# Revit family: Plumbing_Valves_Bermad_720-EN_Pressure_Reducing_Valve Flanged 1.5in-12in
name_source: partatom
category: Pipe Accessories
units: mm (PartAtom-declared; Revit-internal decimal feet)

## family parameters
Always vertical = Yes
Cut with Voids When Loaded = No
Part Type = Valve - Breaks Into
Round Connector Dimension = Use Diameter
Shared = No
Work Plane-Based = No

## types (9) — shared parameters
700EN = Yes
700ES = No
700Grooved = No
700Threaded = No
Act_Ang = 25.00°
Assembly Code = D2020300
D_Table = 700 Revit Sizes
D_Table_Version = 2
Date of publishing = 26/09/2019
Description = Pressure Reducing Valve
HC = No
M = 160 mm
Manufacturer = Bermad
Max Working Water Pressure = 27.6 bar
Max Working Water Temperature = 60 °C
Model = 720
PA = No
PA_8 = No
PB = No
PBL = Yes
Port_Dim = 40 mm  [stored 0.131234 ft]
Product url = www.bermad.com/product/bc-720-p
Show Actuator Maintenance Space = No
T_from_port = 220 mm
URL = www.Bermad.com
Valve Seires = 700 EN

## per-type parameters (varying)
- 1.5" - DN40: Act_BD=127 mm; Ax=6 mm  [stored 0.019685 ft]; Ay=81 mm; Body_Dim=59 mm  [stored 0.19357 ft]; C_Plus=98 mm; D1=86 mm; D2=125 mm; D3=85 mm; D4=125 mm; D5=86 mm; D6=38 mm  [stored 0.124672 ft]; Flange_Dim=155 mm; Flange_Thick=22 mm  [stored 0.0721785 ft]; H=234 mm; H1=10 mm  [stored 0.0328084 ft]; H2=19 mm  [stored 0.062336 ft]; H3=12 mm  [stored 0.0393701 ft]; H4=32 mm  [stored 0.104987 ft]; H5=9 mm  [stored 0.0295276 ft]; K Coefficient=1.9; L=230 mm; L_Half=115 mm; Nominal Diameter=40 mm  [stored 0.131234 ft]; Port_Downx=57 mm  [stored 0.187008 ft]; Port_Upx=57 mm  [stored 0.187008 ft]; Port_W=49 mm  [stored 0.160761 ft]; Port_W2=98 mm; Port_h=44 mm  [stored 0.144357 ft]; W=155 mm; Weight=0.12 kN; h=81 mm
- 2" - DN50: Act_BD=127 mm; Ax=6 mm  [stored 0.019685 ft]; Ay=81 mm; Body_Dim=60 mm  [stored 0.19685 ft]; C_Plus=98 mm; D1=86 mm; D2=125 mm; D3=85 mm; D4=125 mm; D5=86 mm; D6=38 mm  [stored 0.124672 ft]; Flange_Dim=165 mm; Flange_Thick=24 mm  [stored 0.0787402 ft]; H=246 mm; H1=10 mm  [stored 0.0328084 ft]; H2=19 mm  [stored 0.062336 ft]; H3=12 mm  [stored 0.0393701 ft]; H4=32 mm  [stored 0.104987 ft]; H5=9 mm  [stored 0.0295276 ft]; K Coefficient=4.3; L=230 mm; L_Half=115 mm; Nominal Diameter=50 mm  [stored 0.164042 ft]; Port_Downx=60 mm  [stored 0.19685 ft]; Port_Upx=56 mm  [stored 0.183727 ft]; Port_W=49 mm  [stored 0.160761 ft]; Port_W2=98 mm; Port_h=44 mm  [stored 0.144357 ft]; W=165 mm; Weight=0.14 kN; h=86 mm
- 2.5" - DN65: Act_BD=145 mm; Ax=11 mm; Ay=102 mm; Body_Dim=77 mm; C_Plus=108 mm; D1=94 mm; D2=153 mm; D3=131 mm; D4=165 mm; D5=122 mm; D6=42 mm  [stored 0.137795 ft]; Flange_Dim=190 mm; Flange_Thick=27 mm  [stored 0.0885827 ft]; H=294 mm; H1=16 mm  [stored 0.0524934 ft]; H2=28 mm  [stored 0.0918635 ft]; H3=21 mm  [stored 0.0688976 ft]; H4=28 mm  [stored 0.0918635 ft]; H5=23 mm  [stored 0.0754593 ft]; K Coefficient=5.3; L=290 mm; L_Half=145 mm; Nominal Diameter=65 mm  [stored 0.213255 ft]; Port_Downx=71 mm  [stored 0.23294 ft]; Port_Upx=84 mm; Port_W=55 mm  [stored 0.180446 ft]; Port_W2=109 mm; Port_h=59 mm  [stored 0.19357 ft]; W=190 mm; Weight=0.26 kN; h=96 mm
- 3" - DN80: Act_BD=165 mm; Ax=24 mm  [stored 0.0787402 ft]; Ay=126 mm; Body_Dim=100 mm; C_Plus=144 mm; D1=104 mm; D2=153 mm; D3=110 mm; D4=165 mm; D5=124 mm; D6=42 mm  [stored 0.137795 ft]; Flange_Dim=210 mm; Flange_Thick=30 mm  [stored 0.0984252 ft]; H=333 mm; H1=16 mm  [stored 0.0524934 ft]; H2=22 mm  [stored 0.0721785 ft]; H3=22 mm  [stored 0.0721785 ft]; H4=28 mm  [stored 0.0918635 ft]; H5=23 mm  [stored 0.0754593 ft]; K Coefficient=6.2; L=310 mm; L_Half=155 mm; Nominal Diameter=80 mm; Port_Downx=85 mm; Port_Upx=90 mm; Port_W=66 mm  [stored 0.216535 ft]; Port_W2=132 mm; Port_h=60 mm  [stored 0.19685 ft]; W=210 mm; Weight=0.34 kN; h=108 mm
- 4" - DN100: Act_BD=211 mm; Ax=32 mm  [stored 0.104987 ft]; Ay=160 mm; Body_Dim=121 mm; C_Plus=175 mm; D1=132 mm; D2=199 mm; D3=143 mm; D4=200 mm; D5=143 mm; D6=40 mm  [stored 0.131234 ft]; Flange_Dim=255 mm; Flange_Thick=35 mm  [stored 0.114829 ft]; H=396 mm; H1=19 mm  [stored 0.062336 ft]; H2=21 mm  [stored 0.0688976 ft]; H3=26 mm; H4=31 mm  [stored 0.101706 ft]; H5=27 mm  [stored 0.0885827 ft]; K Coefficient=8; L=350 mm; L_Half=175 mm; Nominal Diameter=100 mm; Port_Downx=100 mm; Port_Upx=82 mm; Port_W=103 mm; Port_W2=206 mm; Port_h=70 mm  [stored 0.229659 ft]; W=255 mm; Weight=0.54 kN; h=130 mm
- 6" - DN150: Act_BD=300 mm; Ax=32 mm  [stored 0.104987 ft]; Ay=209 mm; Body_Dim=169 mm; C_Plus=314 mm; D1=196 mm; D2=262 mm; D3=237 mm; D4=320 mm; D5=258 mm; D6=80 mm; Flange_Dim=320 mm; Flange_Thick=38 mm  [stored 0.124672 ft]; H=514 mm; H1=20 mm  [stored 0.0656168 ft]; H2=34 mm; H3=32 mm  [stored 0.104987 ft]; H4=50 mm  [stored 0.164042 ft]; H5=45 mm  [stored 0.147638 ft]; K Coefficient=3.9; L=480 mm; L_Half=240 mm; Nominal Diameter=150 mm; Port_Downx=132 mm; Port_Upx=145 mm; Port_W=104 mm; Port_W2=208 mm; Port_h=95 mm; W=320 mm; Weight=0.94 kN; h=163 mm
- 8" - DN200: Act_BD=311 mm; Ax=20 mm  [stored 0.0656168 ft]; Ay=238 mm; Body_Dim=218 mm; C_Plus=392 mm; D1=249 mm; D2=325 mm; D3=246 mm; D4=390 mm; D5=329 mm; D6=80 mm; Flange_Dim=380 mm; Flange_Thick=43 mm  [stored 0.141076 ft]; H=618 mm; H1=20 mm  [stored 0.0656168 ft]; H2=38 mm  [stored 0.124672 ft]; H3=32 mm  [stored 0.104987 ft]; H4=60 mm  [stored 0.19685 ft]; H5=50 mm  [stored 0.164042 ft]; K Coefficient=4.3; L=600 mm; L_Half=300 mm; Nominal Diameter=200 mm; Port_Downx=170 mm; Port_Upx=170 mm; Port_W=125 mm; Port_W2=250 mm; Port_h=125 mm; W=400 mm; Weight=1.55 kN; h=193 mm
- 10" - DN250: Act_BD=409 mm; Ax=39 mm; Ay=290 mm; Body_Dim=274 mm; C_Plus=507 mm; D1=312 mm; D2=404 mm; D3=352 mm; D4=481 mm; D5=384 mm; D6=120 mm; Flange_Dim=450 mm; Flange_Thick=50 mm  [stored 0.164042 ft]; H=725 mm; H1=24 mm  [stored 0.0787402 ft]; H2=47 mm  [stored 0.154199 ft]; H3=47 mm  [stored 0.154199 ft]; H4=75 mm; H5=43 mm  [stored 0.141076 ft]; K Coefficient=3.6; L=730 mm; L_Half=365 mm; Nominal Diameter=250 mm; Port_Downx=259 mm; Port_Upx=259 mm; Port_W=150 mm; Port_W2=300 mm; Port_h=160 mm; W=480 mm; Weight=2.51 kN; h=227 mm
- 12" - DN300: Act_BD=479 mm; Ax=47 mm  [stored 0.154199 ft]; Ay=344 mm; Body_Dim=327 mm; C_Plus=615 mm; D1=380 mm; D2=461 mm; D3=437 mm; D4=558 mm; D5=444 mm; D6=140 mm; Flange_Dim=530 mm; Flange_Thick=54 mm; H=881 mm; H1=26 mm; H2=57 mm  [stored 0.187008 ft]; H3=55 mm  [stored 0.180446 ft]; H4=87 mm; H5=60 mm  [stored 0.19685 ft]; K Coefficient=3.4; L=850 mm; L_Half=425 mm; Nominal Diameter=300 mm; Port_Downx=319 mm; Port_Upx=319 mm; Port_W=177 mm; Port_W2=354 mm; Port_h=186 mm; W=570 mm; Weight=3.95 kN; h=272 mm

note: [stored X ft] marks values corroborated as IEEE doubles in the binary element streams (Revit-internal decimal feet)

## geometry (parser evidence)
native form markers: Sweep x4
no freeform markers — native parametric forms only
